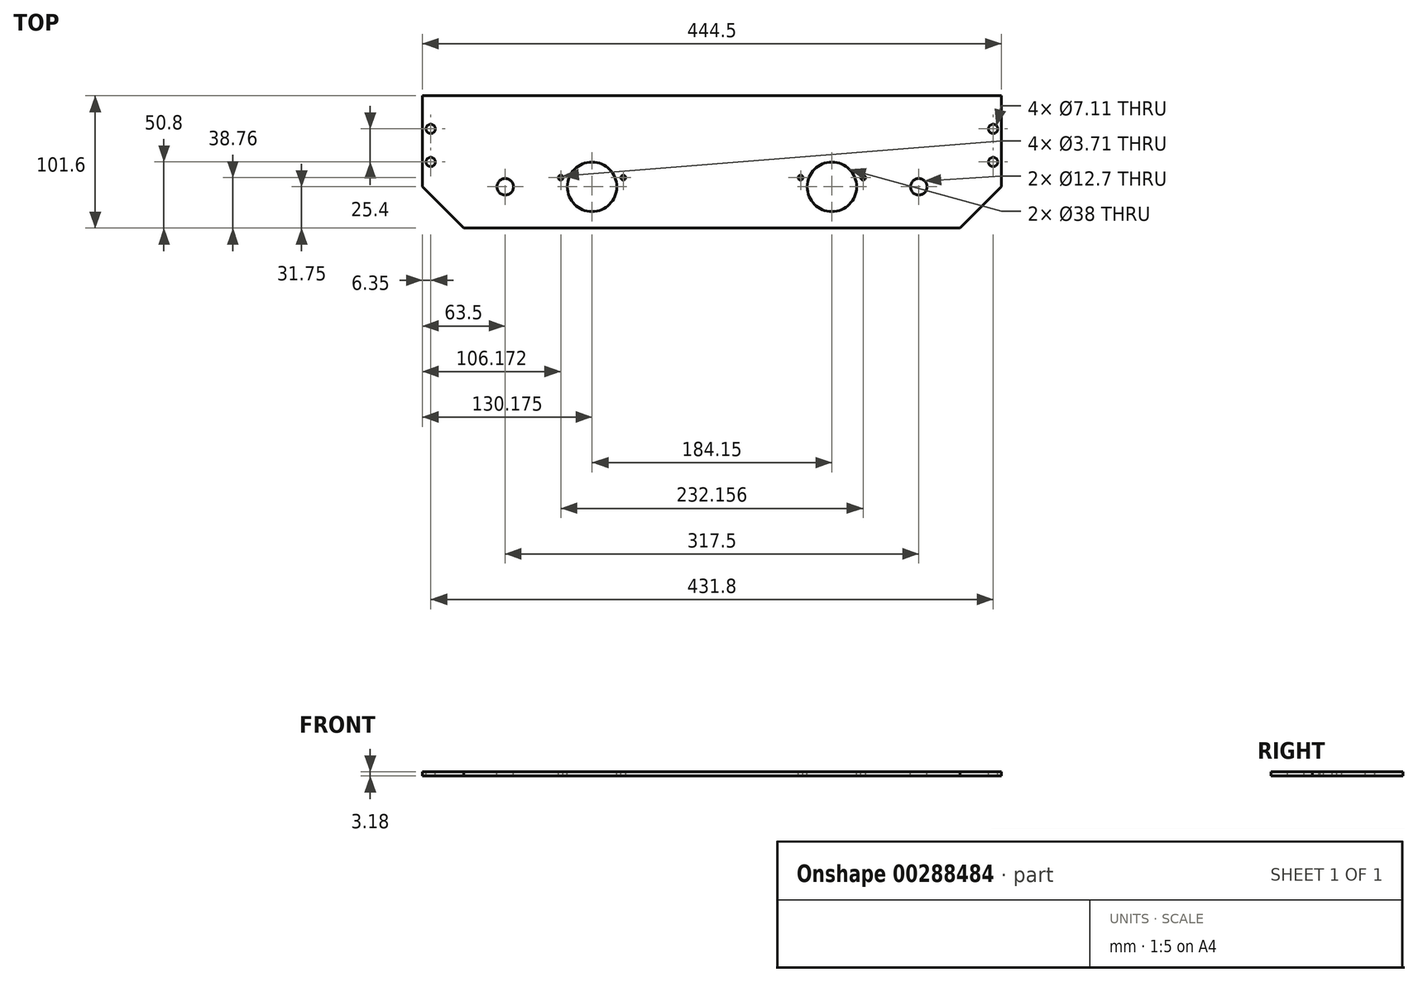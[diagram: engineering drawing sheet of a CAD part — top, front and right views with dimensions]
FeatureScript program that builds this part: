
annotation { "Feature Type Name" : "Feature", "Feature Type Description" : "" }
export const myFeature = defineFeature(function(context is Context, id is Id, definition is map)
    precondition{}
    {
        {
            var Q0;
            Q0=qCreatedBy(makeId("Top.planeOp"),FACE);
            var sketch = newSketch(context, id + "F0", { "sketchPlane" : qUnion([Q0])});
            skLineSegment(sketch, "E0.bottom", {"start": v(0, 101.6) * mm, "end": v(-444.5, 101.6) * mm});
            skLineSegment(sketch, "E0.top", {"start": v(-31.75, 0) * mm, "end": v(-412.75, 0) * mm});
            skLineSegment(sketch, "E0.left", {"start": v(0, 101.6) * mm, "end": v(0, 31.75) * mm});
            skLineSegment(sketch, "E0.right", {"start": v(-444.5, 101.6) * mm, "end": v(-444.5, 31.75) * mm});
            skLineSegment(sketch, "E1", {"start": v(0, 31.75) * mm, "end": v(-31.75, 0) * mm});
            skLineSegment(sketch, "E2", {"start": v(-444.5, 31.75) * mm, "end": v(-412.75, 0) * mm});
            skPoint(sketch, "E3.orphan", {"position": v(-444.5, 0) * mm});
            skLineSegment(sketch, "E4", {"start": v(-444.5, 31.75) * mm, "end": v(0, 31.75) * mm, "construction": true});
            skLineSegment(sketch, "E5", {"start": v(0, 101.6) * mm, "end": v(0, 0) * mm, "construction": true});
            skLineSegment(sketch, "E6", {"start": v(-444.5, 101.6) * mm, "end": v(-444.5, 0) * mm, "construction": true});
            skSolve(sketch);
        }
        {
            var Q0;
            Q0=makeQuery(id+"F0.imprint","IMPRINT",FACE,{"disambiguationData":[TD([[makeQuery(id+"F0.imprint","IMPRINT",EDGE,{"derivedFrom":sQuery(id+"F0.wireOp",EDGE,"E0.bottom")}),1.0]])]});
            extrude(context, id + "F1", {"entities" : qUnion([Q0]), "depth" : 3.17 * mm});
        }
        {
            var Q0;
            Q0=makeQuery(id+"F1.opExtrude","CAP_FACE",FACE,{"disambiguationData":[OSD([sQuery(id+"F0.wireOp",EDGE,"E0.bottom"),sQuery(id+"F0.wireOp",EDGE,"E0.top"),sQuery(id+"F0.wireOp",EDGE,"E0.left"),sQuery(id+"F0.wireOp",EDGE,"E0.right"),sQuery(id+"F0.wireOp",EDGE,"E1"),sQuery(id+"F0.wireOp",EDGE,"E2")])],"isStart":false});
            var sketch = newSketch(context, id + "F2", { "sketchPlane" : qUnion([Q0])});
            skLineSegment(sketch, "E7", {"start": v(-438.15, 101.6) * mm, "end": v(-438.15, 0) * mm, "construction": true});
            skLineSegment(sketch, "E8", {"start": v(-438.15, 101.6) * mm, "end": v(-444.5, 101.6) * mm, "construction": true});
            skPoint(sketch, "E9", {"position": v(-438.15, 76.2) * mm});
            skPoint(sketch, "E10", {"position": v(-438.15, 50.8) * mm});
            skLineSegment(sketch, "E11", {"start": v(-438.15, 76.2) * mm, "end": v(-438.15, 101.6) * mm, "construction": true});
            skLineSegment(sketch, "E12", {"start": v(-438.15, 76.2) * mm, "end": v(-438.15, 50.8) * mm, "construction": true});
            skCircle(sketch, "E13", {"center": v(-438.15, 76.2) * mm, "radius": 3.56 * mm});
            skCircle(sketch, "E14", {"center": v(-438.15, 50.8) * mm, "radius": 3.56 * mm});
            skCircle(sketch, "E15", {"center": v(-381, 31.75) * mm, "radius": 6.35 * mm});
            skCircle(sketch, "E16", {"center": v(-63.5, 31.75) * mm, "radius": 6.35 * mm});
            skLineSegment(sketch, "E17", {"start": v(0, 101.6) * mm, "end": v(-6.35, 101.6) * mm, "construction": true});
            skLineSegment(sketch, "E18", {"start": v(-6.35, 101.6) * mm, "end": v(-6.35, 0) * mm, "construction": true});
            skLineSegment(sketch, "E19", {"start": v(-6.35, 101.6) * mm, "end": v(-6.35, 76.2) * mm, "construction": true});
            skLineSegment(sketch, "E20", {"start": v(-6.35, 76.2) * mm, "end": v(-6.35, 50.8) * mm, "construction": true});
            skCircle(sketch, "E21", {"center": v(-6.35, 76.2) * mm, "radius": 3.56 * mm});
            skCircle(sketch, "E22", {"center": v(-6.35, 50.8) * mm, "radius": 3.56 * mm});
            skSolve(sketch);
        }
        {
            var Q0;
            Q0=makeQuery(id+"F2.imprint","IMPRINT",FACE,{"disambiguationData":[TD([[makeQuery(id+"F2.imprint","IMPRINT",EDGE,{"derivedFrom":sQuery(id+"F2.wireOp",EDGE,"E14")}),1.0]])]});
            extrude(context, id + "F3", {"entities" : qUnion([Q0]), "operationType" : NewBodyOperationType.REMOVE, "oppositeDirection" : true, "depth" : 25.4 * mm});
        }
        {
            var Q0;
            Q0=makeQuery(id+"F2.imprint","IMPRINT",FACE,{"disambiguationData":[TD([[makeQuery(id+"F2.imprint","IMPRINT",EDGE,{"derivedFrom":sQuery(id+"F2.wireOp",EDGE,"E13")}),1.0]])]});
            extrude(context, id + "F4", {"entities" : qUnion([Q0]), "operationType" : NewBodyOperationType.REMOVE, "oppositeDirection" : true, "depth" : 25.4 * mm});
        }
        {
            var Q0;
            Q0=makeQuery(id+"F2.imprint","IMPRINT",FACE,{"disambiguationData":[TD([[makeQuery(id+"F2.imprint","IMPRINT",EDGE,{"derivedFrom":sQuery(id+"F2.wireOp",EDGE,"E15")}),1.0]])]});
            extrude(context, id + "F5", {"entities" : qUnion([Q0]), "operationType" : NewBodyOperationType.REMOVE, "oppositeDirection" : true, "depth" : 25.4 * mm});
        }
        {
            var Q0;
            Q0=makeQuery(id+"F2.imprint","IMPRINT",FACE,{"disambiguationData":[TD([[makeQuery(id+"F2.imprint","IMPRINT",EDGE,{"derivedFrom":sQuery(id+"F2.wireOp",EDGE,"E16")}),1.0]])]});
            extrude(context, id + "F6", {"entities" : qUnion([Q0]), "operationType" : NewBodyOperationType.REMOVE, "oppositeDirection" : true, "depth" : 25.4 * mm});
        }
        {
            var Q0;
            Q0=makeQuery(id+"F2.imprint","IMPRINT",FACE,{"disambiguationData":[TD([[makeQuery(id+"F2.imprint","IMPRINT",EDGE,{"derivedFrom":sQuery(id+"F2.wireOp",EDGE,"E21")}),1.0]])]});
            extrude(context, id + "F7", {"entities" : qUnion([Q0]), "operationType" : NewBodyOperationType.REMOVE, "oppositeDirection" : true, "depth" : 25.4 * mm});
        }
        {
            var Q0;
            Q0=makeQuery(id+"F2.imprint","IMPRINT",FACE,{"disambiguationData":[TD([[makeQuery(id+"F2.imprint","IMPRINT",EDGE,{"derivedFrom":sQuery(id+"F2.wireOp",EDGE,"E22")}),1.0]])]});
            extrude(context, id + "F8", {"entities" : qUnion([Q0]), "operationType" : NewBodyOperationType.REMOVE, "oppositeDirection" : true, "depth" : 25.4 * mm});
        }
        {
            var Q0;
            Q0=makeQuery(id+"F2.imprint","IMPRINT",FACE,{"disambiguationData":[TD([[makeQuery(id+"F2.imprint","IMPRINT",EDGE,{"derivedFrom":sQuery(id+"F2.wireOp",EDGE,"E13")}),-1.0]])]});
            var sketch = newSketch(context, id + "F9", { "sketchPlane" : qUnion([Q0])});
            skLineSegment(sketch, "E23", {"start": v(-743.61, 38.76) * mm, "end": v(340.6, 38.76) * mm, "construction": true});
            skCircle(sketch, "E24", {"center": v(-381, 31.75) * mm, "radius": 66.68 * mm, "construction": true});
            skCircle(sketch, "E25", {"center": v(-314.33, 31.75) * mm, "radius": 19 * mm});
            skLineSegment(sketch, "E26", {"start": v(-314.33, 31.75) * mm, "end": v(-314.33, 82.61) * mm, "construction": true});
            skPoint(sketch, "E27", {"position": v(-314.33, 38.76) * mm});
            skPoint(sketch, "E28", {"position": v(-338.33, 38.76) * mm});
            skCircle(sketch, "E29", {"center": v(-338.33, 38.76) * mm, "radius": 1.85 * mm});
            skPoint(sketch, "E30", {"position": v(-290.32, 38.76) * mm});
            skCircle(sketch, "E31", {"center": v(-290.32, 38.76) * mm, "radius": 1.85 * mm});
            skPoint(sketch, "E32", {"position": v(-130.18, 31.75) * mm});
            skCircle(sketch, "E33", {"center": v(-130.18, 31.75) * mm, "radius": 19 * mm});
            skLineSegment(sketch, "E34", {"start": v(-130.18, 31.75) * mm, "end": v(-130.18, 59.14) * mm, "construction": true});
            skPoint(sketch, "E35", {"position": v(-130.18, 38.76) * mm});
            skPoint(sketch, "E36", {"position": v(-154.18, 38.76) * mm});
            skPoint(sketch, "E37", {"position": v(-106.17, 38.76) * mm});
            skCircle(sketch, "E38", {"center": v(-154.18, 38.76) * mm, "radius": 1.85 * mm});
            skCircle(sketch, "E39", {"center": v(-106.17, 38.76) * mm, "radius": 1.85 * mm});
            skSolve(sketch);
        }
        {
            var Q0;
            Q0 = qSketchRegion(id + "F9", true);
            extrude(context, id + "F10", {"entities" : qUnion([Q0]), "operationType" : NewBodyOperationType.REMOVE, "oppositeDirection" : true, "depth" : 25.4 * mm});
        }
    });
